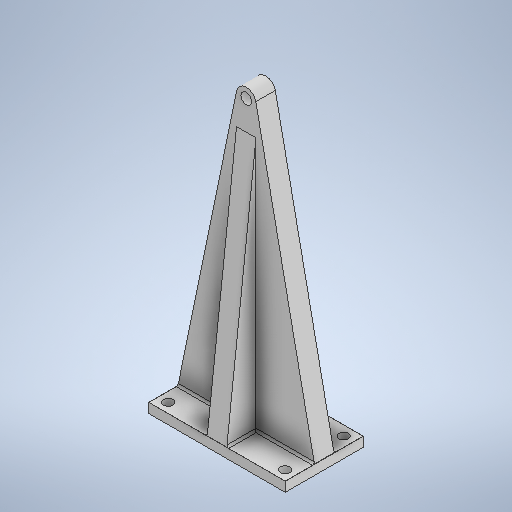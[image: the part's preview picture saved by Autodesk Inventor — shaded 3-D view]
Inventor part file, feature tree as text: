
AUTODESK INVENTOR PART (.ipt)
format: ipt  version: 2025.2 (Build 292293000, 293)  size: 346,112 bytes
history: native  units: mm
features: sketch x9, extrude x6, other x1, mirror x1, fillet x1, hole x1
ambient origin geometry x8: Origin, YZ Plane, XZ Plane, XY Plane, X Axis, Y Axis, Z Axis, Center Point
bodies: Body1 (feature_tree)
feature tree (19):
  other  "Bryła1"
  extrude  "Wyciągnięcie proste1"  Depth=70.0mm
  extrude  "Wyciągnięcie proste6"  Depth=40.0mm
  extrude  "Wyciągnięcie proste7"  Depth=5.0mm TaperAngle=0.0deg
  sketch  "Szkic10"
  extrude  "Wyciągnięcie proste8"  Depth=70.0mm
  sketch  "Szkic12"
  extrude  "Wyciągnięcie proste9"  Depth=10.0mm
  extrude  "Wyciągnięcie proste10"  Depth=150.0mm TaperAngle=0.0deg
  mirror  "Odbij1"
  fillet  "Zaokrąglenie1"  Radius=5.5mm
  hole  "Otwór1"  [1 undecoded]
  sketch  "Szkic1"
  sketch  "Szkic8"
  sketch  "Szkic9"
  sketch  "Szkic11"
  sketch  "Szkic13"
  sketch  "Szkic14"
  sketch  "Szkic16"
note: 1 required parameter value undecoded (feature->parameter linkage not recoverable at this tier; creation-order binding heuristic only, values carry confidence <= 0.55)
